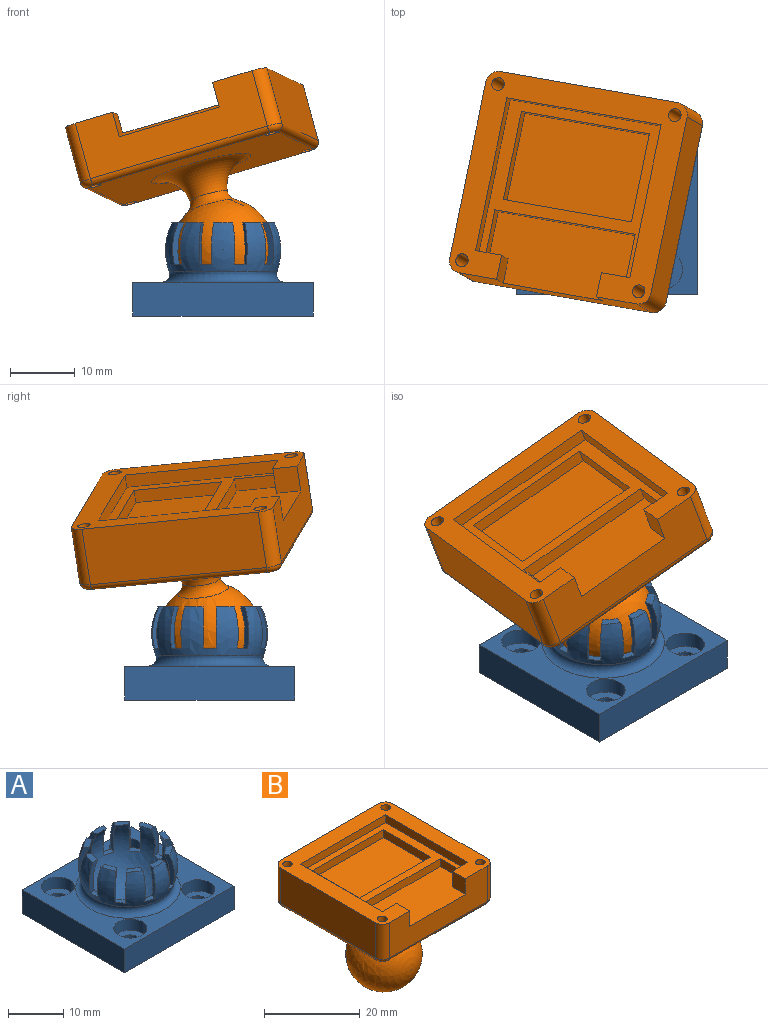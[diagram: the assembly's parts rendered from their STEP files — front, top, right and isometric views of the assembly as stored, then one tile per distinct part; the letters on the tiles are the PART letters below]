
ASSEMBLY  parts=2 mates=1
PART A: 61 faces, bbox 28x26.3x19.3 mm
  f0: cylinder r=1.5mm len=3mm, axis (0,0,-1), area 25.9mm2, adj f19,f59
  f1: cylinder r=1.5mm len=3mm, axis (0,0,-1), area 25.9mm2, adj f19,f57
  f2: cylinder r=1.5mm len=3mm, axis (0,0,-1), area 25.9mm2, adj f19,f55
  f3: cylinder r=1.5mm len=3mm, axis (0,0,-1), area 25.9mm2, adj f19,f53
  f4: sphere r=9mm, area 291.8mm2, adj f5,f6,f7,f8,f9,f10,f11,f12
  f5: plane 2.85x1.86mm, normal (0,0,1), area 3mm2, adj f4,f14,f25,f28
  f6: plane 2.78x2.44mm, normal (0,0,1), area 3mm2, adj f4,f14,f49,f51
  f7: plane 2.85x1.86mm, normal (0,0,1), area 3mm2, adj f4,f14,f24,f50
  f8: plane 2.78x2.44mm, normal (0,0,1), area 3mm2, adj f4,f14,f43,f45
  f9: plane 3x1.24mm, normal (0,0,1), area 3mm2, adj f4,f14,f46,f48
  f10: plane 2.85x1.86mm, normal (0,0,1), area 3mm2, adj f4,f14,f37,f39
  f11: plane 2.85x1.86mm, normal (0,0,1), area 3mm2, adj f4,f14,f40,f42
  f12: plane 3x1.24mm, normal (0,0,1), area 3mm2, adj f4,f14,f31,f33
  f13: plane 2.78x2.44mm, normal (0,0,1), area 3mm2, adj f4,f14,f34,f36
  f14: sphere r=8mm, area 476.6mm2, adj f5,f6,f7,f8,f9,f10,f11,f12
  f15: plane 2.78x2.44mm, normal (0,0,1), area 3mm2, adj f4,f14,f27,f30
  f16: plane 28x5.25mm, normal (0,1,0), area 147.1mm2, adj f17,f19,f20,f21
  f17: plane 28x26.35mm, normal (0,0,1), area 341.7mm2, adj f16,f18,f20,f21,f22,f54,f56,f58
  f18: plane 28x5.25mm, normal (0,-1,0), area 147.1mm2, adj f17,f19,f20,f21
  f19: plane 28x26.35mm, normal (0,0,-1), area 709.5mm2, adj f0,f1,f2,f3,f16,f18,f20,f21
  f20: plane 26.35x5.25mm, normal (1,0,0), area 138.4mm2, adj f16,f17,f18,f19
  f21: plane 26.35x5.25mm, normal (-1,0,0), area 138.4mm2, adj f16,f17,f18,f19
  f22: torus R=9.49mm, axis (0,0,-1), area 130.5mm2, adj f4,f17
  f23: plane 2x1.1mm, normal (0,0,1), area 2.1mm2, adj f4,f14,f24,f25
  f24: plane 6.4x2.17mm, normal (0,-1,0), area 6.7mm2, adj f4,f7,f14,f23
  f25: plane 6.4x2.17mm, normal (0,1,0), area 6.7mm2, adj f4,f5,f14,f23
  f26: plane 2.23x2.02mm, normal (0,0,1), area 2.1mm2, adj f4,f14,f27,f28
  f27: plane 6.4x1.75mm, normal (0.59,0.81,0), area 6.7mm2, adj f4,f14,f15,f26
  f28: plane 6.4x1.75mm, normal (-0.59,-0.81,0), area 6.7mm2, adj f4,f5,f14,f26
  f29: plane 2.23x1.61mm, normal (0,0,1), area 2.1mm2, adj f4,f14,f30,f31
  f30: plane 6.4x2.06mm, normal (-0.95,-0.31,0), area 6.7mm2, adj f4,f14,f15,f29
  f31: plane 6.4x2.06mm, normal (0.95,0.31,0), area 6.7mm2, adj f4,f12,f14,f29
  f32: plane 2.23x1.61mm, normal (0,0,1), area 2.1mm2, adj f4,f14,f33,f34
  f33: plane 6.4x2.06mm, normal (-0.95,0.31,0), area 6.7mm2, adj f4,f12,f14,f32
  f34: plane 6.4x2.06mm, normal (0.95,-0.31,0), area 6.7mm2, adj f4,f13,f14,f32
  f35: plane 2.23x2.02mm, normal (0,0,1), area 2.1mm2, adj f4,f14,f36,f37
  f36: plane 6.4x1.75mm, normal (-0.59,0.81,0), area 6.7mm2, adj f4,f13,f14,f35
  f37: plane 6.4x1.75mm, normal (0.59,-0.81,0), area 6.7mm2, adj f4,f10,f14,f35
  f38: plane 2x1.1mm, normal (0,0,1), area 2.1mm2, adj f4,f14,f39,f40
  f39: plane 6.4x2.17mm, normal (0,1,0), area 6.7mm2, adj f4,f10,f14,f38
  f40: plane 6.4x2.17mm, normal (0,-1,0), area 6.7mm2, adj f4,f11,f14,f38
  f41: plane 2.23x2.02mm, normal (0,0,1), area 2.1mm2, adj f4,f14,f42,f43
  f42: plane 6.4x1.75mm, normal (0.59,0.81,0), area 6.7mm2, adj f4,f11,f14,f41
  f43: plane 6.4x1.75mm, normal (-0.59,-0.81,0), area 6.7mm2, adj f4,f8,f14,f41
  f44: plane 2.23x1.61mm, normal (0,0,1), area 2.1mm2, adj f4,f14,f45,f46
  f45: plane 6.4x2.06mm, normal (0.95,0.31,0), area 6.7mm2, adj f4,f8,f14,f44
  f46: plane 6.4x2.06mm, normal (-0.95,-0.31,0), area 6.7mm2, adj f4,f9,f14,f44
  f47: plane 2.23x1.61mm, normal (0,0,1), area 2.1mm2, adj f4,f14,f48,f49
  f48: plane 6.4x2.06mm, normal (0.95,-0.31,0), area 6.7mm2, adj f4,f9,f14,f47
  f49: plane 6.4x2.06mm, normal (-0.95,0.31,0), area 6.7mm2, adj f4,f6,f14,f47
  f50: plane 6.4x1.75mm, normal (-0.59,0.81,0), area 6.7mm2, adj f4,f7,f14,f52
  f51: plane 6.4x1.75mm, normal (0.59,-0.81,0), area 6.7mm2, adj f4,f6,f14,f52
  f52: plane 2.23x2.02mm, normal (0,0,1), area 2.1mm2, adj f4,f14,f50,f51
  f53: plane 6x6mm, normal (0,0,1), area 21.2mm2, adj f3,f54
  f54: cylinder r=3mm len=6mm, axis (0,0,1), area 47.1mm2, adj f17,f53
  f55: plane 6x6mm, normal (0,0,1), area 21.2mm2, adj f2,f56
  f56: cylinder r=3mm len=6mm, axis (0,0,1), area 47.1mm2, adj f17,f55
  f57: plane 6x6mm, normal (0,0,1), area 21.2mm2, adj f1,f58
  f58: cylinder r=3mm len=6mm, axis (0,0,1), area 47.1mm2, adj f17,f57
  f59: plane 6x6mm, normal (0,0,1), area 21.2mm2, adj f0,f60
  f60: cylinder r=3mm len=6mm, axis (0,0,1), area 47.1mm2, adj f17,f59
PART B: 42 faces, bbox 33.3x32.3x31.2 mm
  f0: plane 29x9mm, normal (0,-1,0), area 195.4mm2, adj f1,f16,f17,f20,f30,f33,f35
  f1: plane 33x32mm, normal (0,0,1), area 362.1mm2, adj f0,f4,f5,f6,f7,f8,f9,f10
  f2: sphere r=8mm, area 751.1mm2, adj f3
  f3: torus R=4.94mm, axis (0,0,-1), area 42.8mm2, adj f2,f12
  f4: plane 28x9mm, normal (1,0,0), area 252mm2, adj f1,f30,f31,f39
  f5: plane 29x9mm, normal (0,1,0), area 261mm2, adj f1,f31,f32,f40
  f6: cylinder r=1mm len=10mm, axis (0,0,-1), area 62.8mm2, adj f1,f11,f37
  f7: cylinder r=1mm len=10mm, axis (0,0,-1), area 62.8mm2, adj f1,f11,f34
  f8: cylinder r=1mm len=10mm, axis (0,0,-1), area 62.8mm2, adj f1,f11,f38
  f9: cylinder r=1mm len=10mm, axis (0,0,-1), area 62.8mm2, adj f1,f11,f41
  f10: plane 28x9mm, normal (-1,0,0), area 252mm2, adj f1,f32,f33,f36
  f11: plane 31x30mm, normal (0,0,-1), area 716.4mm2, adj f6,f7,f8,f9,f12,f35,f36,f39
  f12: torus R=7.98mm, axis (0,0,1), area 228.8mm2, adj f3,f11
  f13: plane 23x2mm, normal (0,-1,0), area 46mm2, adj f14,f19,f20,f24
  f14: plane 7x2mm, normal (1,0,0), area 14mm2, adj f13,f15,f20,f24
  f15: plane 4.25x4mm, normal (0,1,0), area 14.7mm2, adj f1,f14,f16,f20,f23,f24
  f16: plane 4x3.85mm, normal (1,0,0), area 15.4mm2, adj f0,f1,f15,f20
  f17: plane 4x3.85mm, normal (-1,0,0), area 15.4mm2, adj f0,f1,f18,f20
  f18: plane 4.65x4mm, normal (0,1,0), area 16.3mm2, adj f1,f17,f19,f20,f21,f24
  f19: plane 7x2mm, normal (-1,0,0), area 14mm2, adj f13,f18,f20,f24
  f20: plane 23x10.85mm, normal (0,0,1), area 224.1mm2, adj f0,f13,f14,f15,f16,f17,f18,f19
  f21: plane 24.3x2mm, normal (-1,0,0), area 48.6mm2, adj f1,f18,f22,f24
  f22: plane 25.3x2mm, normal (0,-1,0), area 50.6mm2, adj f1,f21,f23,f24
  f23: plane 24.3x2mm, normal (1,0,0), area 48.6mm2, adj f1,f15,f22,f24
  f24: plane 25.3x24.3mm, normal (0,0,1), area 159.8mm2, adj f13,f14,f15,f18,f19,f21,f22,f23
  f25: plane 21x14mm, normal (0,0,1), area 294mm2, adj f26,f27,f28,f29
  f26: plane 14x2mm, normal (1,0,0), area 28mm2, adj f24,f25,f27,f29
  f27: plane 21x2mm, normal (0,-1,0), area 42mm2, adj f24,f25,f26,f28
  f28: plane 14x2mm, normal (-1,0,0), area 28mm2, adj f24,f25,f27,f29
  f29: plane 21x2mm, normal (0,1,0), area 42mm2, adj f24,f25,f26,f28
  f30: cylinder r=2mm len=9mm, axis (0,0,-1), area 28.3mm2, adj f0,f1,f4,f37
  f31: cylinder r=2mm len=9mm, axis (0,0,1), area 28.3mm2, adj f1,f4,f5,f41
  f32: cylinder r=2mm len=9mm, axis (0,0,-1), area 28.3mm2, adj f1,f5,f10,f38
  f33: cylinder r=2mm len=9mm, axis (0,0,1), area 28.3mm2, adj f0,f1,f10,f34
  f34: torus R=1mm, axis (0,0,1), area 4mm2, adj f7,f33,f35,f36
  f35: cylinder r=1mm len=29mm, axis (1,0,0), area 45.6mm2, adj f0,f11,f34,f37
  f36: cylinder r=1mm len=28mm, axis (0,-1,0), area 44mm2, adj f10,f11,f34,f38
  f37: torus R=1mm, axis (0,0,1), area 4mm2, adj f6,f30,f35,f39
  f38: torus R=1mm, axis (0,0,1), area 4mm2, adj f8,f32,f36,f40
  f39: cylinder r=1mm len=28mm, axis (0,1,0), area 44mm2, adj f4,f11,f37,f41
  f40: cylinder r=1mm len=29mm, axis (-1,0,0), area 45.6mm2, adj f5,f11,f38,f41
  f41: torus R=1mm, axis (0,0,1), area 4mm2, adj f9,f31,f39,f40
PLACE A t=(-1.84,-21.89,10.55)mm fixed
PLACE B rot(axis=(-0.35,-0.78,-0.53),20.4deg) t=(-1.84,-21.89,-7.55)mm
MATE ball B.f3 <-> A.f22  axis (-0.26,0.15,0.95) through (-1.84,-21.89,-7.55)mm
